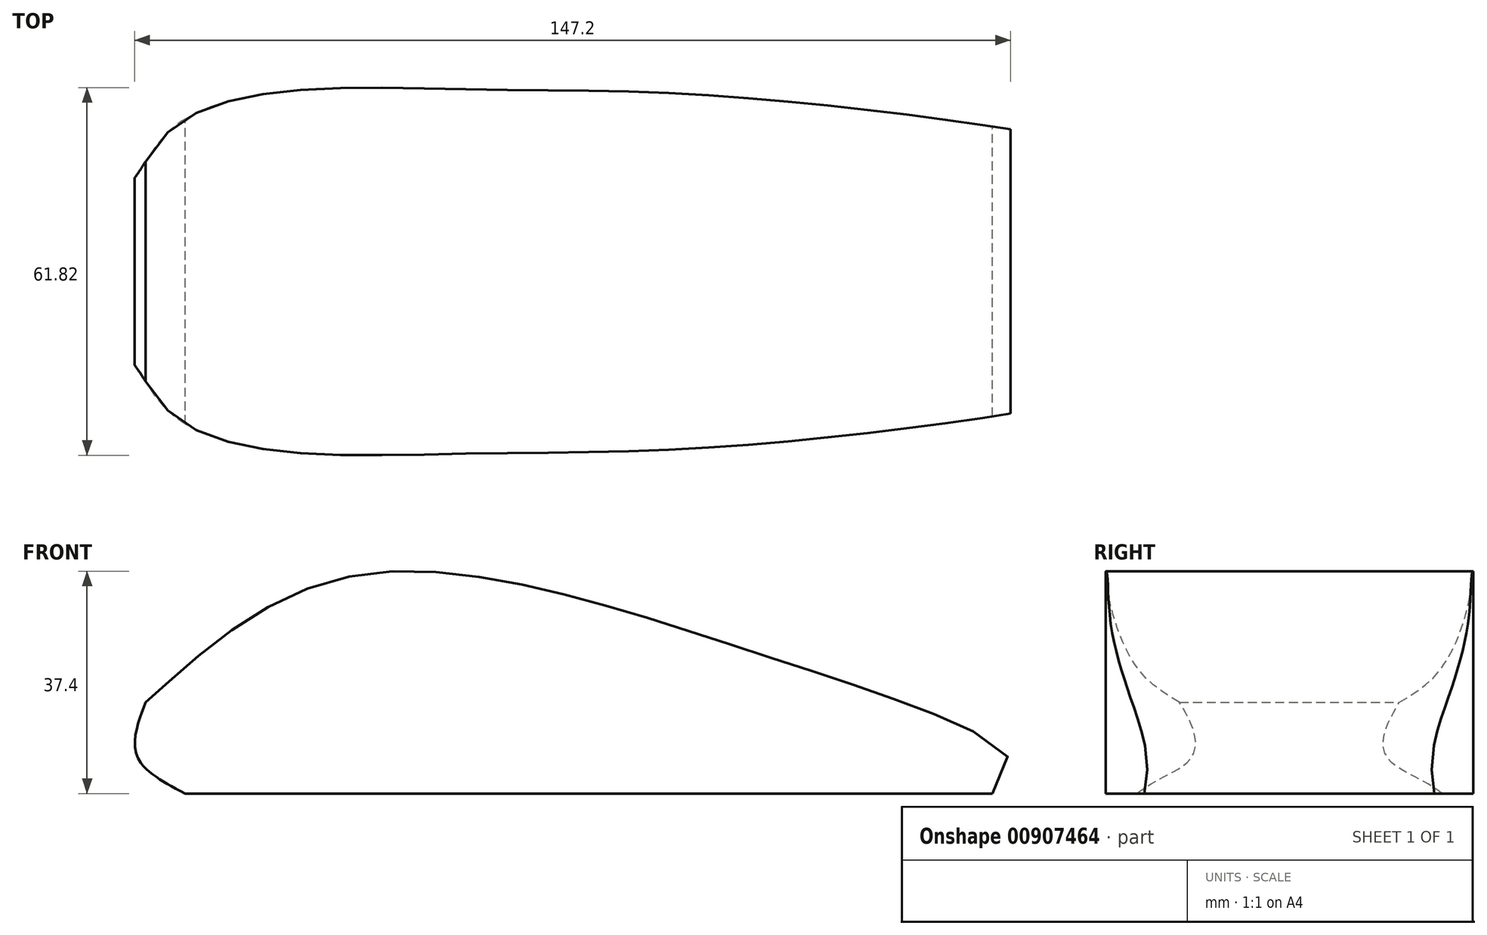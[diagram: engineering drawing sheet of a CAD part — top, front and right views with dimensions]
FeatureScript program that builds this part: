
annotation { "Feature Type Name" : "Feature", "Feature Type Description" : "" }
export const myFeature = defineFeature(function(context is Context, id is Id, definition is map)
    precondition{}
    {
        {
            var Q0;
            Q0=qCreatedBy(makeId("Front.planeOp"),FACE);
            var sketch = newSketch(context, id + "F0", { "sketchPlane" : qUnion([Q0])});
            skFitSpline(sketch, "E0", {"points": [v(-77.98, 15.34) * mm, v(-42.4, 36.75) * mm, v(27.06, 22.86) * mm, v(67.28, 5.5) * mm, v(64.38, 0) * mm], "startDerivative": vector(117.64, 105.99) * mm, "endDerivative": vector(-51.29, -51.75) * mm});
            skFitSpline(sketch, "E1", {"points": [v(64.38, 0) * mm, v(-71.33, 0) * mm], "startDerivative": vector(-135.71, 0) * mm, "endDerivative": vector(-135.71, 0) * mm});
            skFitSpline(sketch, "E2", {"points": [v(-71.33, 0) * mm, v(-79.43, 6.37) * mm, v(-77.98, 15.34) * mm], "startDerivative": vector(-20.53, 10.75) * mm, "endDerivative": vector(7.52, 20.02) * mm});
            skSolve(sketch);
        }
        {
            var Q0;
            Q0=makeQuery(id+"F0.imprint","IMPRINT",FACE,{"disambiguationData":[TD([[makeQuery(id+"F0.imprint","IMPRINT",EDGE,{"derivedFrom":sQuery(id+"F0.wireOp",EDGE,"E0")}),-1.0]])]});
            extrude(context, id + "F1", {"entities" : qUnion([Q0]), "endBound" : BoundingType.SYMMETRIC, "depth" : 66.04 * mm, "offsetDistance" : 25.4 * mm});
        }
        {
            var Q0;
            Q0=qCreatedBy(makeId("Top.planeOp"),FACE);
            var sketch = newSketch(context, id + "F2", { "sketchPlane" : qUnion([Q0])});
            skFitSpline(sketch, "E3", {"points": [v(70.31, 23.44) * mm, v(13.89, 29.8) * mm, v(-25.76, 30.67) * mm, v(-73.21, 24.3) * mm, v(-83.05, 13.89) * mm, v(-96.07, 44.56) * mm, v(-36.46, 64.53) * mm, v(82.47, 53.24) * mm, v(94.91, 24.3) * mm, v(70.31, 23.44) * mm]});
            skFitSpline(sketch, "E4.MirrorC", {"points": [v(70.31, -23.44) * mm, v(13.89, -29.8) * mm, v(-25.76, -30.67) * mm, v(-73.21, -24.3) * mm, v(-83.05, -13.89) * mm, v(-96.07, -44.56) * mm, v(-36.46, -64.53) * mm, v(82.47, -53.24) * mm, v(94.91, -24.3) * mm, v(70.31, -23.44) * mm]});
            skSolve(sketch);
        }
        {
            var Q0;
            Q0=makeQuery(id+"F2.imprint","IMPRINT",FACE,{"disambiguationData":[TD([[makeQuery(id+"F2.imprint","IMPRINT",EDGE,{"derivedFrom":sQuery(id+"F2.wireOp",EDGE,"E3")}),-1.0]])]});
            var Q1;
            Q1=makeQuery(id+"F2.imprint","IMPRINT",FACE,{"disambiguationData":[TD([[makeQuery(id+"F2.imprint","IMPRINT",EDGE,{"derivedFrom":sQuery(id+"F2.wireOp",EDGE,"E4.MirrorC")}),1.0]])]});
            extrude(context, id + "F3", {"entities" : qUnion([Q0, Q1]), "operationType" : NewBodyOperationType.REMOVE, "depth" : 46.23 * mm, "offsetDistance" : 25.4 * mm});
        }
    });
